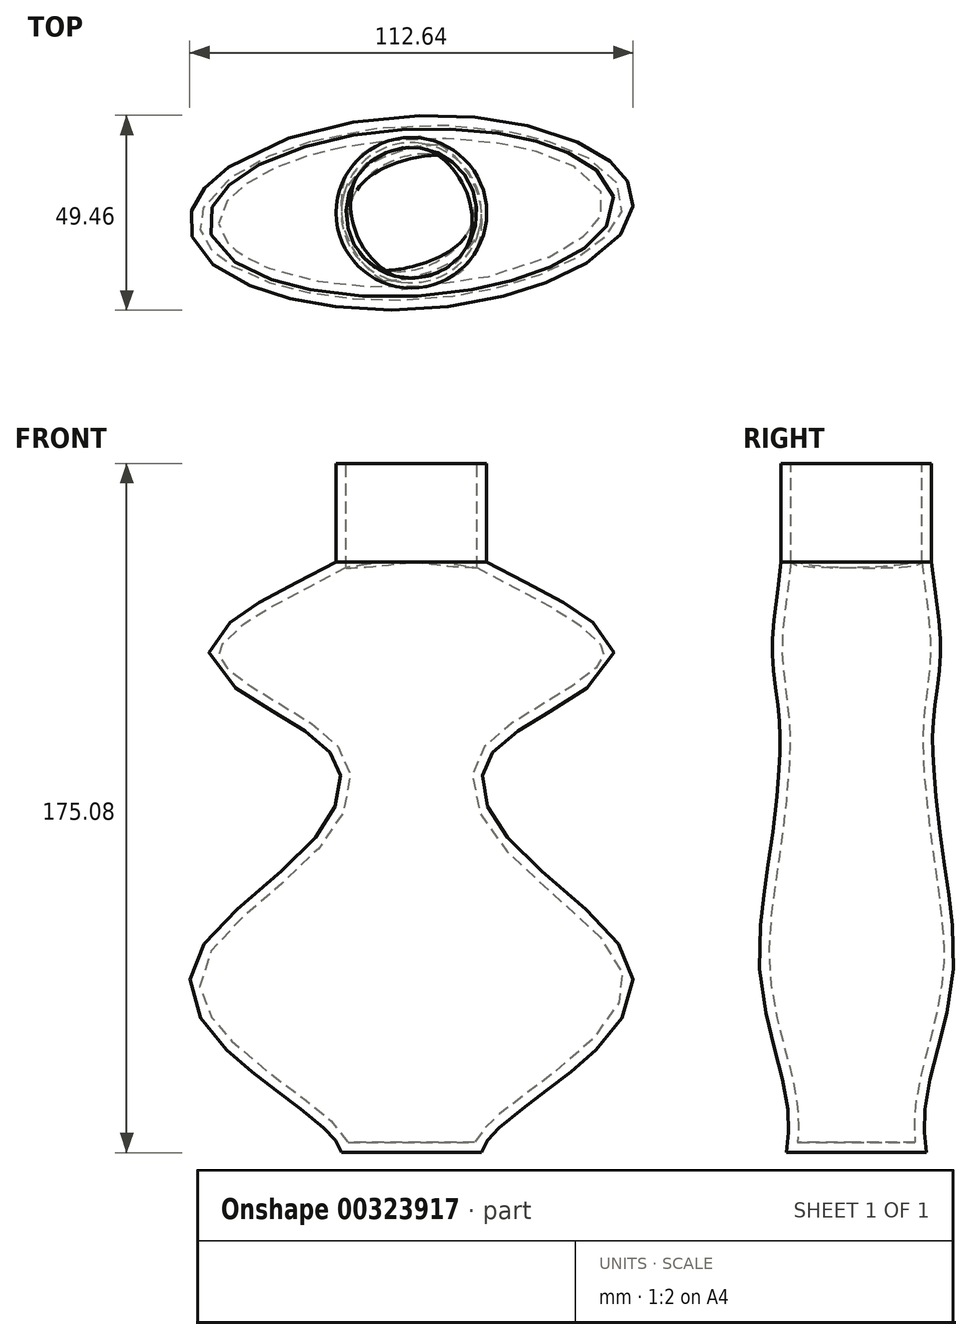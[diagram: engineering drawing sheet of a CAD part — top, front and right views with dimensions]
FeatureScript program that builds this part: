
annotation { "Feature Type Name" : "Feature", "Feature Type Description" : "" }
export const myFeature = defineFeature(function(context is Context, id is Id, definition is map)
    precondition{}
    {
        {
            var Q0;
            Q0=qCreatedBy(makeId("Top.planeOp"),FACE);
            cPlane(context, id + "F0", {"entities" : qUnion([Q0]), "cplaneType" : CPlaneType.OFFSET, "offset" : 50 * mm, "width" : 152.4 * mm, "height" : 152.4 * mm});
        }
        {
            var Q0;
            Q0=qCreatedBy(id+"F0.planeOp",FACE);
            var sketch = newSketch(context, id + "F1", { "sketchPlane" : qUnion([Q0])});
            skEllipse(sketch, "E0", {"center": v(0, 0) * mm, "majorRadius": 54.6 * mm, "minorRadius": 24.58 * mm, "majorAxis": v(1, 0.06)});
            skSolve(sketch);
        }
        {
            var Q0;
            Q0=qCreatedBy(id+"F0.planeOp",FACE);
            cPlane(context, id + "F2", {"entities" : qUnion([Q0]), "cplaneType" : CPlaneType.OFFSET, "offset" : 25 * mm, "width" : 150 * mm, "height" : 150 * mm});
        }
        {
            var Q0;
            Q0=qCreatedBy(id+"F2.planeOp",FACE);
            cPlane(context, id + "F3", {"entities" : qUnion([Q0]), "cplaneType" : CPlaneType.OFFSET, "offset" : 25 * mm, "width" : 150 * mm, "height" : 150 * mm});
        }
        {
            var Q0;
            Q0=qCreatedBy(id+"F3.planeOp",FACE);
            var sketch = newSketch(context, id + "F4", { "sketchPlane" : qUnion([Q0])});
            skCircle(sketch, "E1", {"center": v(0, 0) * mm, "radius": 19.47 * mm});
            skSolve(sketch);
        }
        {
            var Q0;
            Q0=qCreatedBy(id+"F3.planeOp",FACE);
            cPlane(context, id + "F5", {"entities" : qUnion([Q0]), "cplaneType" : CPlaneType.OFFSET, "offset" : 25 * mm, "width" : 150 * mm, "height" : 150 * mm});
        }
        {
            var Q0;
            Q0=qCreatedBy(id+"F5.planeOp",FACE);
            var sketch = newSketch(context, id + "F6", { "sketchPlane" : qUnion([Q0])});
            skEllipse(sketch, "E2", {"center": v(0, 0) * mm, "majorRadius": 51.26 * mm, "minorRadius": 21.11 * mm, "majorAxis": v(1, 0.06)});
            skSolve(sketch);
        }
        {
            var Q0;
            Q0=qCreatedBy(id+"F5.planeOp",FACE);
            cPlane(context, id + "F7", {"entities" : qUnion([Q0]), "cplaneType" : CPlaneType.OFFSET, "offset" : 25 * mm, "width" : 150 * mm, "height" : 150 * mm});
        }
        {
            var Q0;
            Q0=qCreatedBy(id+"F7.planeOp",FACE);
            var sketch = newSketch(context, id + "F8", { "sketchPlane" : qUnion([Q0])});
            skCircle(sketch, "E3", {"center": v(0, 0) * mm, "radius": 19.12 * mm});
            skSolve(sketch);
        }
        {
            var Q0;
            Q0=qCreatedBy(makeId("Top.planeOp"),FACE);
            var sketch = newSketch(context, id + "F9", { "sketchPlane" : qUnion([Q0])});
            skCircle(sketch, "E4", {"center": v(0, 0) * mm, "radius": 17.81 * mm});
            skSolve(sketch);
        }
        {
            var Q0;
            Q0 = qSketchRegion(id + "F9", true);
            var Q1;
            Q1 = qSketchRegion(id + "F1", true);
            var Q2;
            Q2 = qSketchRegion(id + "F4", true);
            var Q3;
            Q3 = qSketchRegion(id + "F6", true);
            var Q4;
            Q4 = qSketchRegion(id + "F8", true);
            loft(context, id + "F10", {"sheetProfilesArray" : [{ "sheetProfileEntities" : qUnion([Q0]) }, { "sheetProfileEntities" : qUnion([Q1]) }, { "sheetProfileEntities" : qUnion([Q2]) }, { "sheetProfileEntities" : qUnion([Q3]) }, { "sheetProfileEntities" : qUnion([Q4]) }]});
        }
        {
            var Q0;
            Q0=makeQuery(id+"F10.opLoft","CAP_FACE",FACE,{"disambiguationData":[OSD([makeQuery(id+"F8.imprint","IMPRINT",FACE,{"disambiguationData":[TD([[makeQuery(id+"F8.imprint","IMPRINT",EDGE,{"derivedFrom":sQuery(id+"F8.wireOp",EDGE,"E3")}),1.0]])]})])],"isStart":true});
            extrude(context, id + "F11", {"entities" : qUnion([Q0]), "operationType" : NewBodyOperationType.ADD, "depth" : 25 * mm});
        }
        {
            var Q0;
            Q0=makeQuery(id+"F11.opExtrude","CAP_FACE",FACE,{"disambiguationData":[OSD([makeQuery(id+"F8.imprint","IMPRINT",FACE,{"disambiguationData":[TD([[makeQuery(id+"F8.imprint","IMPRINT",EDGE,{"derivedFrom":sQuery(id+"F8.wireOp",EDGE,"E3")}),1.0]])]})])],"isStart":false});
            shell(context, id + "F12", {"entities" : qUnion([Q0]), "thickness" : 2.5 * mm});
        }
    });
